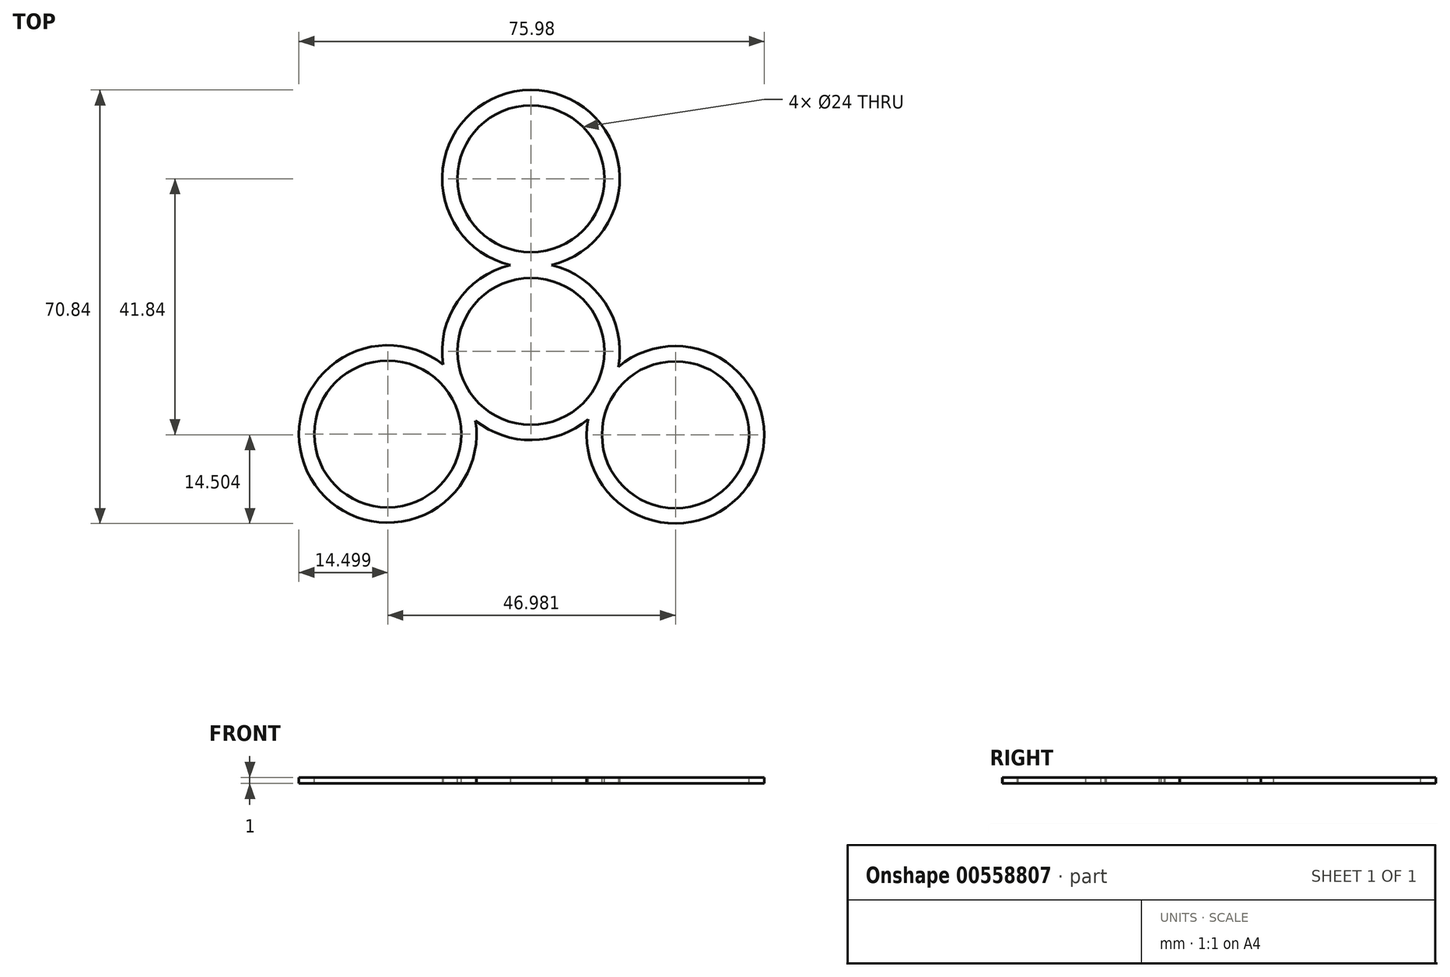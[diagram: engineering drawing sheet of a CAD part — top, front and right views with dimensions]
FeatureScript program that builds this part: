
annotation { "Feature Type Name" : "Feature", "Feature Type Description" : "" }
export const myFeature = defineFeature(function(context is Context, id is Id, definition is map)
    precondition{}
    {
        {
            var Q0;
            Q0=qCreatedBy(makeId("Top.planeOp"),FACE);
            var sketch = newSketch(context, id + "F0", { "sketchPlane" : qUnion([Q0])});
            skCircle(sketch, "E0", {"center": v(-0.18, -2.17) * mm, "radius": 11 * mm});
            skLineSegment(sketch, "E1", {"start": v(-0.18, -1.43) * mm, "end": v(-0.18, 8.83) * mm});
            skLineSegment(sketch, "E2", {"start": v(-0.18, 8.83) * mm, "end": v(-0.18, 10.04) * mm});
            skLineSegment(sketch, "E3", {"start": v(-0.18, 13.83) * mm, "end": v(-0.18, 15.04) * mm});
            skCircle(sketch, "E4", {"center": v(-23.56, -15.67) * mm, "radius": 11 * mm});
            skCircle(sketch, "E5", {"center": v(23.42, -15.8) * mm, "radius": 11 * mm});
            skCircle(sketch, "E6", {"center": v(-0.18, 26.04) * mm, "radius": 11 * mm});
            skArc(sketch, "E7.0", {"start": v(-9.22, -13.5) * mm, "mid": v(0, -16.67) * mm, "end": v(9.14, -13.28) * mm});
            skArc(sketch, "E8.0", {"start": v(-14.52, -4.34) * mm, "mid": v(-36.12, -22.92) * mm, "end": v(-9.22, -13.5) * mm});
            skArc(sketch, "E9.0", {"start": v(9.14, -13.28) * mm, "mid": v(35.98, -23.05) * mm, "end": v(14.1, -4.69) * mm});
            skArc(sketch, "E10.0", {"start": v(3.17, 11.94) * mm, "mid": v(-0.18, 40.54) * mm, "end": v(-3.53, 11.94) * mm});
            skArc(sketch, "E11.trimOffspring", {"start": v(14.1, -4.69) * mm, "mid": v(11.94, 5.8) * mm, "end": v(3.17, 11.94) * mm});
            skArc(sketch, "E12.trimOffspring", {"start": v(-3.53, 11.94) * mm, "mid": v(-12.2, 5.94) * mm, "end": v(-14.52, -4.34) * mm});
            skSolve(sketch);
        }
        {
            var Q0;
            Q0 = qSketchRegion(id + "F0", true);
            extrude(context, id + "F1", {"entities" : qUnion([Q0]), "depth" : 1 * mm, "offsetDistance" : 25 * mm});
        }
        {
            var Q0;
            Q0=makeQuery(id+"F1.opExtrude","CAP_FACE",FACE,{"disambiguationData":[OSD([sQuery(id+"F0.wireOp",EDGE,"E0"),sQuery(id+"F0.wireOp",EDGE,"E4"),sQuery(id+"F0.wireOp",EDGE,"E5"),sQuery(id+"F0.wireOp",EDGE,"E6"),sQuery(id+"F0.wireOp",EDGE,"E7.0"),sQuery(id+"F0.wireOp",EDGE,"E8.0"),sQuery(id+"F0.wireOp",EDGE,"E9.0"),sQuery(id+"F0.wireOp",EDGE,"E10.0"),sQuery(id+"F0.wireOp",EDGE,"E11.trimOffspring"),sQuery(id+"F0.wireOp",EDGE,"E12.trimOffspring")])],"isStart":false});
            var sketch = newSketch(context, id + "F2", { "sketchPlane" : qUnion([Q0])});
            skCircle(sketch, "E13.0", {"center": v(-0.18, 26.04) * mm, "radius": 12 * mm});
            skCircle(sketch, "E14.0", {"center": v(-0.18, -2.17) * mm, "radius": 12 * mm});
            skCircle(sketch, "E15.0", {"center": v(23.42, -15.8) * mm, "radius": 12 * mm});
            skCircle(sketch, "E16.0", {"center": v(-23.56, -15.67) * mm, "radius": 12 * mm});
            skSolve(sketch);
        }
        {
            var Q0;
            Q0 = qSketchRegion(id + "F2", true);
            extrude(context, id + "F3", {"entities" : qUnion([Q0]), "operationType" : NewBodyOperationType.REMOVE, "oppositeDirection" : true, "depth" : 25 * mm, "offsetDistance" : 25 * mm});
        }
    });
